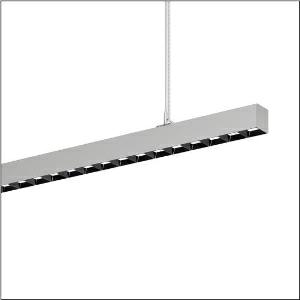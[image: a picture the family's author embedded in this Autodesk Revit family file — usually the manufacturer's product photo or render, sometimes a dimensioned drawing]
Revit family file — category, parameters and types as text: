
# Revit family: silica_r__21_51mx34dc4dsb_5451
name_source: partatom
category: Lighting Fixtures
units: mm (PartAtom-declared; Revit-internal decimal feet)

## family parameters
Cut with Voids When Loaded = No
Host = Face
Light Source = No
Part Type = Normal
Room Calculation Point = No
Round Connector Dimension = Use Diameter
Shared = No

## types (1)
- --- (1 x LED, 19200 lm, 120.3 W, 4000K)
    Apparent Load = 120 VA
    CIE Flux Codes = 74 94 99 56 100
    Color Rendering = 80
    Color Temperature = 4000K
    Default Elevation = 1800 mm
    Description = Silica® 21, office luminaire, primary light control with darklight reflector, of PMMA, black, light emission: direct/indirect distribution, primary light characteristic: asymmetric, installation type: suspended mounting, LED, rated luminous flux: 19.200lm, luminous efficacy: 160lm/W, light colour: 840, colour temperature: 4000K, with terminal, 3+2-pole, max. 2.5mm², mains connection: 220..240V, AC, 50/60Hz, rated input power: 120.3W, luminaire housing, of aluminium, metallic grey (RAL 9006), length: 3.004mm, width: 53mm, height: 53mm, protection rating (complete): IP20, insulation class (complete): insulation class I (protective earthing), certification: CE, permissible operating ambient temperature: 0..+35°C, standard: EN 50419, packaging unit: 1 piece
    Height = 53 mm
    Lamp = 1 x LED
    Lamp Light Flux = 19200 lm
    Lamp Power = 120.3 W
    Lamp count = 1
    Length = 3004 mm
    Luminous efficacy = 160 lm/W
    Manufacturer = Siteco
    ModVariant = No
    Model = 51MX34DC4DSB
    Mounting Place = Ceiling
    Mounting Type = Pendant
    Number of Poles = 1
    OnlyDefault = Yes
    Power Factor = 1
    Product Name = Silica® 21
    Product group = office luminaire | ceiling pendant
    ProductGroupID = 902
    Protection Class = Protection class I
    Protection Degree = IP 20
    RLX_Detail_Level = 1
    RLX_Emergency_Light_Flux = 0 lm
    RLX_Emergency_Type = 0
    RLX_Emergency_Type_DB = No
    RlxData = <blob elided: 67429 chars, md5=aa5f08cd>
    Socket = socket
    Standby Power = 0 W
    System Light Flux = 19200 lm
    System Power = 120 W
    Type Comments = factory setting: luminous flux: 100 % | dim-lin: 254 | 418 mA
    Type Image = l_1335859.jpg
    URL = http://relux.com
    VarID = @adj_089387
    Voltage = 0 V
    Weight = 0.00 kg
    Width = 53 mm

## geometry (parser evidence)
native form markers: Blend x4, Sweep x10
no freeform markers — native parametric forms only
